# Revit family: 506_VCE-C-_-E-ZP-0-0
name_source: partatom
category: Electrical Equipment
revit_build: Autodesk Revit 2018 (Build: 20170223_1515(x64)
units: mm (PartAtom-declared; Revit-internal decimal feet)

## family parameters
Always vertical = Yes
Cut with Voids When Loaded = No
Part Type = Equipment Switch
Room Calculation Point = No
Round Connector Dimension = Use Diameter
Shared = No
Work Plane-Based = No

## types (3) — shared parameters
Description = Air curtain ESSENSSE, ouput series C, electric heater
H = 240 mm  [stored 0.787402 ft]
MC Active Power = 1 W
MC CosPhi = 0.95
MC Number of Poles = 3
MC Voltage = 0 V
MT1 = No
MT2 = Yes
Manufacturer = 2VV
PHR = 20 mm  [stored 0.0656168 ft]
PHS = 20 mm  [stored 0.0656168 ft]
R1 = 120 mm  [stored 0.393701 ft]
URL = www.2vv.cz
W2 = 216 mm
W3 = 96 mm
Y1 = 20 mm  [stored 0.0656168 ft]
magiApparentLoad = 1 VA
magiPartTypeId = 506
magiProductFamilyId = VCE-C-*-E-ZP-0-0
zero-valued in all types: L2D, W2D

## per-type parameters (varying)
| type | L | L2 | L3 | L__ve |
| VCE-C-100-E-ZP-0-0 | 1075 mm  [stored 3.5269 ft] | 538 mm | 488 mm | -1075 mm  [stored -3.5269 ft] |
| VCE-C-200-E-ZP-0-0 | 2077 mm | 1039 mm | 989 mm | -2077 mm |
| VCE-C-150-E-ZP-0-0 | 1577 mm | 789 mm | 739 mm | -1577 mm |

note: column(s) folded — value = type name in every type: MC Product Code, magiProductId

note: [stored X ft] marks values corroborated as IEEE doubles in the binary element streams (Revit-internal decimal feet)

## geometry (parser evidence)
native form markers: Blend x2, Sweep x2
no freeform markers — native parametric forms only
